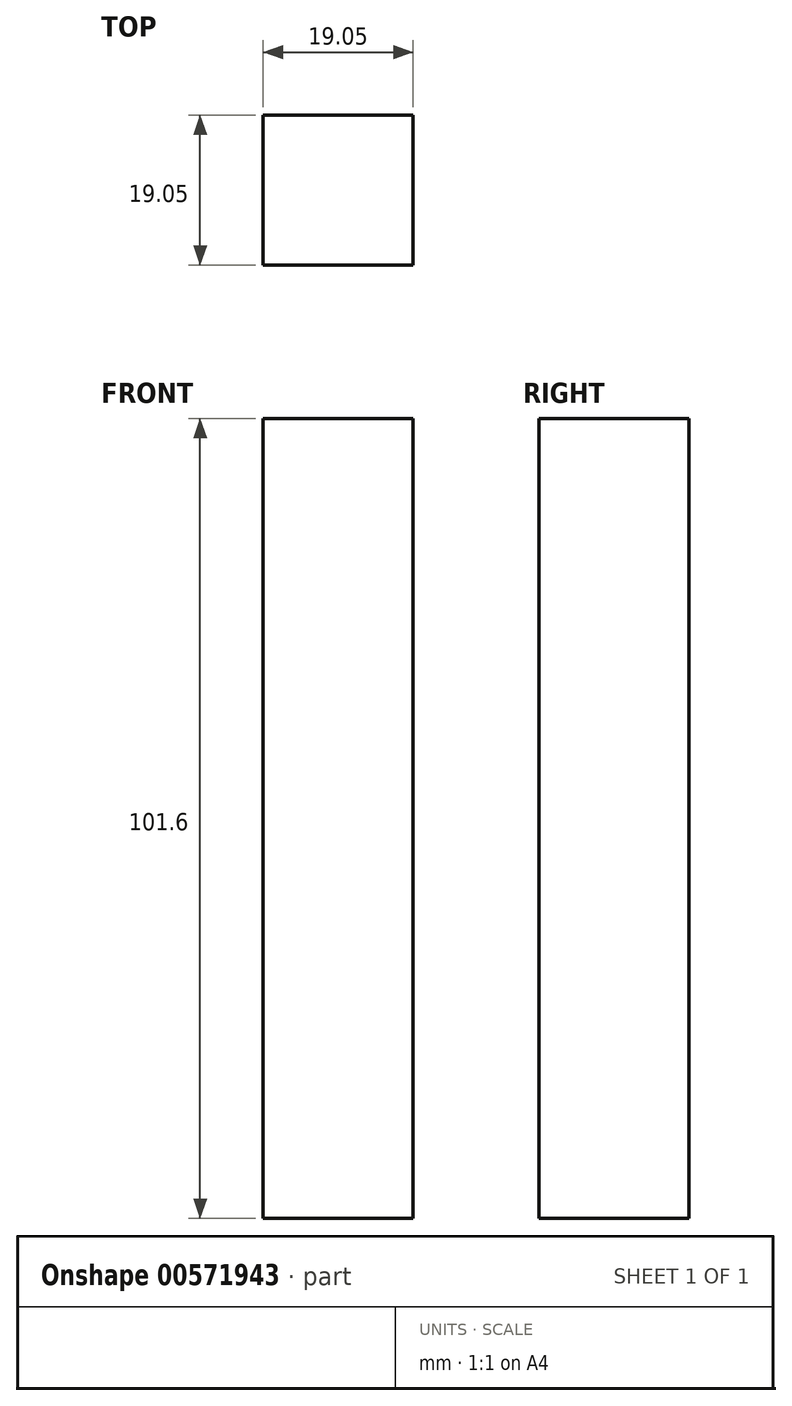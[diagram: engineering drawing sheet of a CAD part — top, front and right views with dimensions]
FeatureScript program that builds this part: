
annotation { "Feature Type Name" : "Feature", "Feature Type Description" : "" }
export const myFeature = defineFeature(function(context is Context, id is Id, definition is map)
    precondition{}
    {
        {
            var Q0;
            Q0=qCreatedBy(makeId("Front.planeOp"),FACE);
            var sketch = newSketch(context, id + "F0", { "sketchPlane" : qUnion([Q0])});
            skLineSegment(sketch, "E0.bottom", {"start": v(0, 0) * mm, "end": v(-19.05, 0) * mm});
            skLineSegment(sketch, "E0.top", {"start": v(0, 101.6) * mm, "end": v(-19.05, 101.6) * mm});
            skLineSegment(sketch, "E0.left", {"start": v(0, 0) * mm, "end": v(0, 101.6) * mm});
            skLineSegment(sketch, "E0.right", {"start": v(-19.05, 0) * mm, "end": v(-19.05, 101.6) * mm});
            skSolve(sketch);
        }
        {
            var Q0;
            Q0 = qSketchRegion(id + "F0", true);
            extrude(context, id + "F1", {"entities" : qUnion([Q0]), "depth" : 19.05 * mm, "offsetDistance" : 25.4 * mm});
        }
    });
